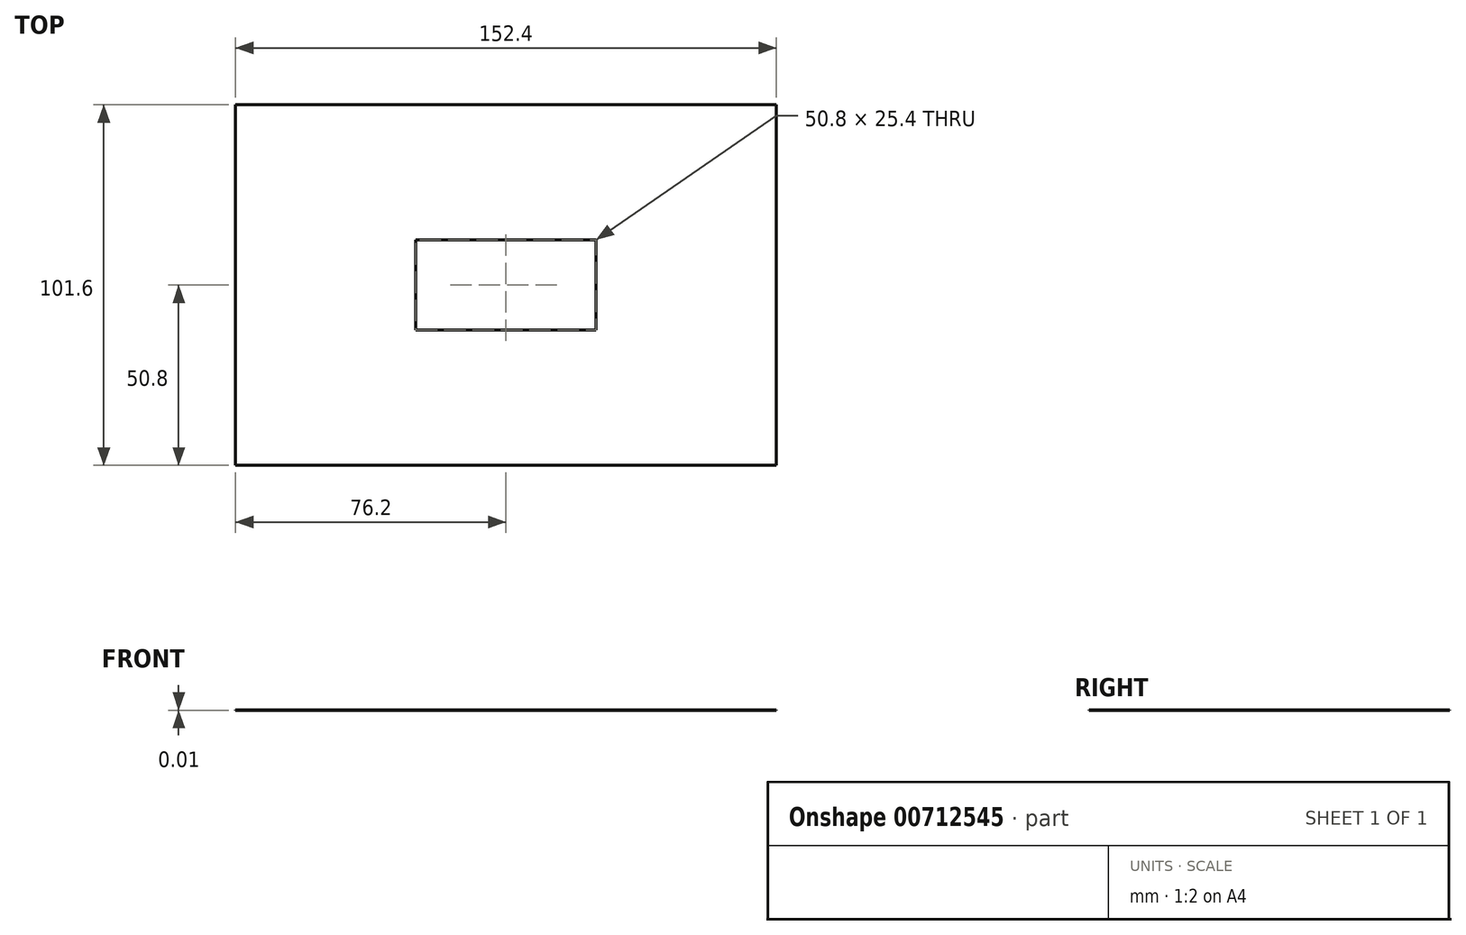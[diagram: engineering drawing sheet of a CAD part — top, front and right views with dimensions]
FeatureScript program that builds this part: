
annotation { "Feature Type Name" : "Feature", "Feature Type Description" : "" }
export const myFeature = defineFeature(function(context is Context, id is Id, definition is map)
    precondition{}
    {
        {
            var Q0;
            Q0=qCreatedBy(makeId("Top.planeOp"),FACE);
            var sketch = newSketch(context, id + "F0", { "sketchPlane" : qUnion([Q0])});
            skLineSegment(sketch, "E0.bottom", {"start": v(76.2, -50.8) * mm, "end": v(-76.2, -50.8) * mm});
            skLineSegment(sketch, "E0.top", {"start": v(76.2, 50.8) * mm, "end": v(-76.2, 50.8) * mm});
            skLineSegment(sketch, "E0.left", {"start": v(76.2, -50.8) * mm, "end": v(76.2, 50.8) * mm});
            skLineSegment(sketch, "E0.right", {"start": v(-76.2, -50.8) * mm, "end": v(-76.2, 50.8) * mm});
            skPoint(sketch, "E0.middle", {"position": v(0, 0) * mm});
            skPoint(sketch, "E1.middle", {"position": v(0, -50.8) * mm});
            skLineSegment(sketch, "E2.bottom", {"start": v(-25.4, -12.7) * mm, "end": v(25.4, -12.7) * mm});
            skLineSegment(sketch, "E2.top", {"start": v(-25.4, 12.7) * mm, "end": v(25.4, 12.7) * mm});
            skLineSegment(sketch, "E2.left", {"start": v(-25.4, -12.7) * mm, "end": v(-25.4, 12.7) * mm});
            skLineSegment(sketch, "E2.right", {"start": v(25.4, -12.7) * mm, "end": v(25.4, 12.7) * mm});
            skSolve(sketch);
        }
        {
            var Q0;
            Q0=makeQuery(id+"F0.imprint","IMPRINT",FACE,{"disambiguationData":[TD([[makeQuery(id+"F0.imprint","IMPRINT",EDGE,{"derivedFrom":sQuery(id+"F0.wireOp",EDGE,"E0.top")}),1.0]])]});
            extrude(context, id + "F1", {"entities" : qUnion([Q0]), "depth" : 3 / 203.2 * mm, "offsetDistance" : 25.4 * mm});
        }
    });
